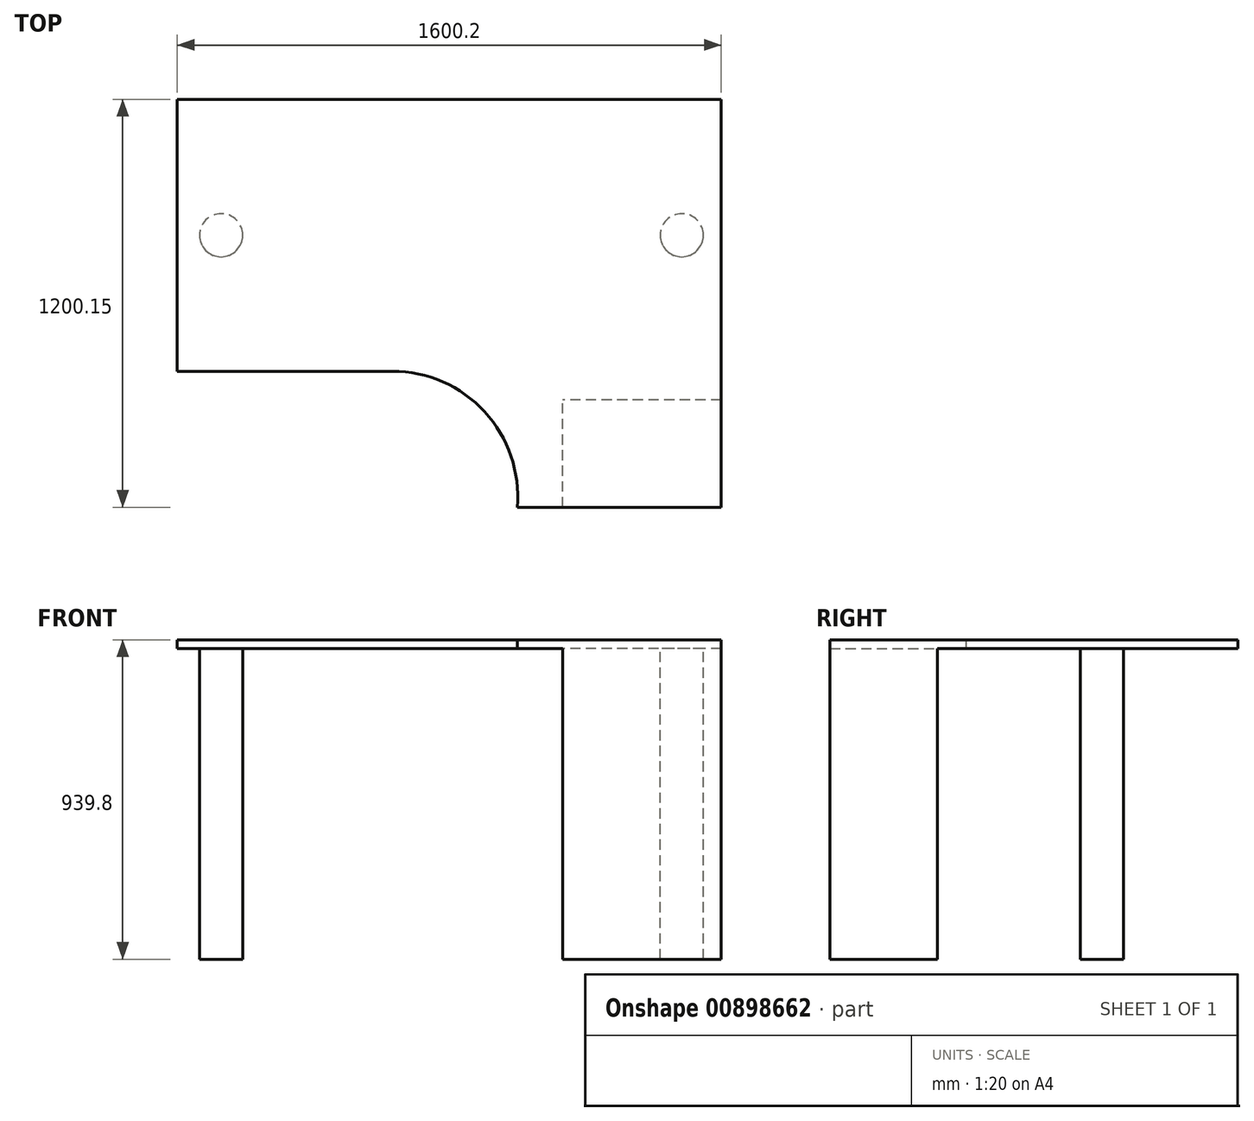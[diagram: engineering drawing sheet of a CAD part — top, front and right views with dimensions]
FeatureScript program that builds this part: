
annotation { "Feature Type Name" : "Feature", "Feature Type Description" : "" }
export const myFeature = defineFeature(function(context is Context, id is Id, definition is map)
    precondition{}
    {
        {
            var Q0;
            Q0=qCreatedBy(makeId("Top.planeOp"),FACE);
            var sketch = newSketch(context, id + "F0", { "sketchPlane" : qUnion([Q0])});
            skLineSegment(sketch, "E0", {"start": v(-632.86, 0) * mm, "end": v(-632.86, 800.1) * mm});
            skLineSegment(sketch, "E1", {"start": v(-632.86, 800.1) * mm, "end": v(967.34, 800.1) * mm});
            skLineSegment(sketch, "E2", {"start": v(967.34, 800.1) * mm, "end": v(967.34, -400.05) * mm});
            skLineSegment(sketch, "E3", {"start": v(967.34, -400.05) * mm, "end": v(367.27, -400.05) * mm});
            skArc(sketch, "E4", {"start": v(367.27, -400.05) * mm, "mid": v(271.53, -119.33) * mm, "end": v(0, 0) * mm});
            skLineSegment(sketch, "E5", {"start": v(0, 0) * mm, "end": v(-632.86, 0) * mm});
            skSolve(sketch);
        }
        {
            var Q0;
            Q0=makeQuery(id+"F0.imprint","IMPRINT",FACE,{"disambiguationData":[TD([[makeQuery(id+"F0.imprint","IMPRINT",EDGE,{"derivedFrom":sQuery(id+"F0.wireOp",EDGE,"E0")}),-1.0]])]});
            extrude(context, id + "F1", {"entities" : qUnion([Q0]), "depth" : 25.4 * mm, "offsetDistance" : 25.4 * mm});
        }
        {
            var Q0;
            Q0=makeQuery(id+"F1.opExtrude","CAP_FACE",FACE,{"disambiguationData":[OSD([sQuery(id+"F0.wireOp",EDGE,"E0"),sQuery(id+"F0.wireOp",EDGE,"E1"),sQuery(id+"F0.wireOp",EDGE,"E2"),sQuery(id+"F0.wireOp",EDGE,"E3"),sQuery(id+"F0.wireOp",EDGE,"E4"),sQuery(id+"F0.wireOp",EDGE,"E5")])],"isStart":true});
            var sketch = newSketch(context, id + "F2", { "sketchPlane" : qUnion([Q0])});
            skLineSegment(sketch, "E6.bottom", {"start": v(967.34, 400.05) * mm, "end": v(500.8, 400.05) * mm});
            skLineSegment(sketch, "E6.top", {"start": v(967.34, 83.9) * mm, "end": v(500.8, 83.9) * mm});
            skLineSegment(sketch, "E6.left", {"start": v(967.34, 400.05) * mm, "end": v(967.34, 83.9) * mm});
            skLineSegment(sketch, "E6.right", {"start": v(500.8, 400.05) * mm, "end": v(500.8, 83.9) * mm});
            skCircle(sketch, "E7", {"center": v(-503.78, -400.05) * mm, "radius": 63.5 * mm});
            skCircle(sketch, "E8", {"center": v(851.41, -400.05) * mm, "radius": 63.5 * mm});
            skLineSegment(sketch, "E9", {"start": v(-632.86, -400.05) * mm, "end": v(967.34, -400.05) * mm});
            skSolve(sketch);
        }
        {
            var Q0;
            {var subQ0=sQuery(id+"F2.wireOp",EDGE,"E9");var subQ1=sQuery(id+"F2.wireOp",EDGE,"E7");var subQ2=makeQuery(id+"F2.imprint","INTERSECT",VERTEX,{"disambiguationData":[OD(0.0)],"derivedFrom":[subQ1,subQ0]});Q0=makeQuery(id+"F2.imprint","IMPRINT",FACE,{"disambiguationData":[TD([[makeQuery(id+"F2.imprint","IMPRINT",EDGE,{"disambiguationData":[TD([[subQ2,1.0]])],"derivedFrom":subQ1}),1.0]])]});}
            var Q1;
            {var subQ0=sQuery(id+"F2.wireOp",EDGE,"E9");var subQ1=sQuery(id+"F2.wireOp",EDGE,"E7");var subQ2=makeQuery(id+"F2.imprint","INTERSECT",VERTEX,{"disambiguationData":[OD(0.0)],"derivedFrom":[subQ1,subQ0]});Q1=makeQuery(id+"F2.imprint","IMPRINT",FACE,{"disambiguationData":[TD([[makeQuery(id+"F2.imprint","IMPRINT",EDGE,{"disambiguationData":[TD([[subQ2,-1.0]])],"derivedFrom":subQ1}),1.0]])]});}
            var Q2;
            {var subQ0=sQuery(id+"F2.wireOp",EDGE,"E9");var subQ1=sQuery(id+"F2.wireOp",EDGE,"E8");var subQ2=makeQuery(id+"F2.imprint","INTERSECT",VERTEX,{"disambiguationData":[OD(0.0)],"derivedFrom":[subQ1,subQ0]});Q2=makeQuery(id+"F2.imprint","IMPRINT",FACE,{"disambiguationData":[TD([[makeQuery(id+"F2.imprint","IMPRINT",EDGE,{"disambiguationData":[TD([[subQ2,1.0]])],"derivedFrom":subQ1}),1.0]])]});}
            var Q3;
            {var subQ0=sQuery(id+"F2.wireOp",EDGE,"E9");var subQ1=sQuery(id+"F2.wireOp",EDGE,"E8");var subQ2=makeQuery(id+"F2.imprint","INTERSECT",VERTEX,{"disambiguationData":[OD(0.0)],"derivedFrom":[subQ1,subQ0]});Q3=makeQuery(id+"F2.imprint","IMPRINT",FACE,{"disambiguationData":[TD([[makeQuery(id+"F2.imprint","IMPRINT",EDGE,{"disambiguationData":[TD([[subQ2,-1.0]])],"derivedFrom":subQ1}),1.0]])]});}
            var Q4;
            Q4=makeQuery(id+"F2.imprint","IMPRINT",FACE,{"disambiguationData":[TD([[makeQuery(id+"F2.imprint","IMPRINT",EDGE,{"derivedFrom":sQuery(id+"F2.wireOp",EDGE,"E6.bottom")}),1.0]])]});
            extrude(context, id + "F3", {"entities" : qUnion([Q0, Q1, Q2, Q3, Q4]), "operationType" : NewBodyOperationType.ADD, "depth" : 914.4 * mm, "offsetDistance" : 25.4 * mm});
        }
    });
